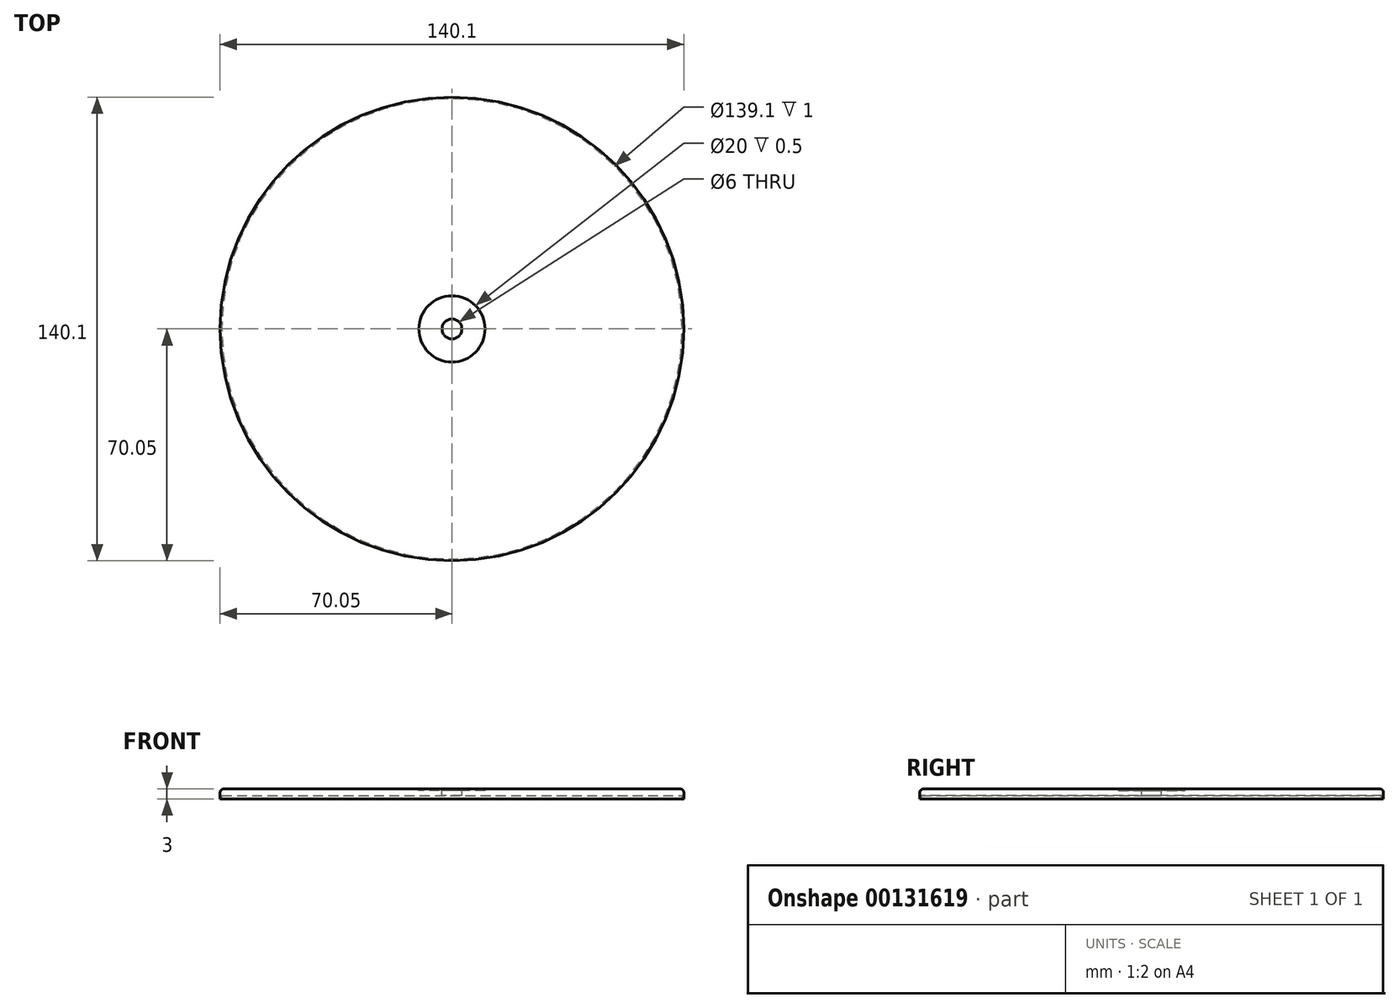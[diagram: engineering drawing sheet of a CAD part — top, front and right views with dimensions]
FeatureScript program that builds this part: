
annotation { "Feature Type Name" : "Feature", "Feature Type Description" : "" }
export const myFeature = defineFeature(function(context is Context, id is Id, definition is map)
    precondition{}
    {
        {
            var Q0;
            Q0=qCreatedBy(makeId("Top.planeOp"),FACE);
            var sketch = newSketch(context, id + "F0", { "sketchPlane" : qUnion([Q0])});
            skCircle(sketch, "E0", {"center": v(0, 0) * mm, "radius": 70.05 * mm});
            skSolve(sketch);
        }
        {
            var Q0;
            Q0=qSketchRegion(id+"F0",true);
            extrude(context, id + "F1", {"entities" : qUnion([Q0]), "depth" : 2 * mm});
        }
        {
            var Q0;
            Q0=makeQuery(id+"F1.opExtrude","CAP_EDGE",EDGE,{"disambiguationData":[OSD([sQuery(id+"F0.wireOp",EDGE,"E0")])],"isStart":false});
            fillet(context, id + "F2", {"entities" : qUnion([Q0]), "radius" : 1 * mm, "tangentPropagation" : true, "allowEdgeOverflow" : false});
        }
        {
            var Q0;
            Q0=makeQuery(id+"F1.opExtrude","CAP_FACE",FACE,{"disambiguationData":[OSD([sQuery(id+"F0.wireOp",EDGE,"E0")])],"isStart":true});
            var sketch = newSketch(context, id + "F3", { "sketchPlane" : qUnion([Q0])});
            skCircle(sketch, "E1", {"center": v(0, 0) * mm, "radius": 70.05 * mm});
            skCircle(sketch, "E2", {"center": v(0, 0) * mm, "radius": 69.55 * mm});
            skSolve(sketch);
        }
        {
            var Q0;
            Q0 = qSketchRegion(id + "F3", true);
            extrude(context, id + "F4", {"entities" : qUnion([Q0]), "operationType" : NewBodyOperationType.ADD, "depth" : 1 * mm});
        }
        {
            var Q0;
            Q0=makeQuery(id+"F1.opExtrude","CAP_FACE",FACE,{"disambiguationData":[OSD([sQuery(id+"F0.wireOp",EDGE,"E0")])],"isStart":false});
            var sketch = newSketch(context, id + "F5", { "sketchPlane" : qUnion([Q0])});
            skCircle(sketch, "E3", {"center": v(0, 0) * mm, "radius": 10 * mm});
            skSolve(sketch);
        }
        {
            var Q0;
            Q0 = qSketchRegion(id + "F5", true);
            extrude(context, id + "F6", {"entities" : qUnion([Q0]), "operationType" : NewBodyOperationType.REMOVE, "oppositeDirection" : true, "depth" : .5 * mm});
        }
        {
            var Q0;
            Q0=makeQuery(id+"F6.boolean.opBoolean","COPY",FACE,{"derivedFrom":makeQuery(id+"F6.opExtrude","CAP_FACE",FACE,{"disambiguationData":[OSD([sQuery(id+"F5.wireOp",EDGE,"E3")])],"isStart":false})});
            var sketch = newSketch(context, id + "F7", { "sketchPlane" : qUnion([Q0])});
            skCircle(sketch, "E4", {"center": v(0, 0) * mm, "radius": 3 * mm});
            skSolve(sketch);
        }
        {
            var Q0;
            Q0 = qSketchRegion(id + "F7", true);
            extrude(context, id + "F8", {"entities" : qUnion([Q0]), "operationType" : NewBodyOperationType.REMOVE, "endBound" : BoundingType.UP_TO_NEXT, "oppositeDirection" : true, "depth" : 25 * mm});
        }
    });
